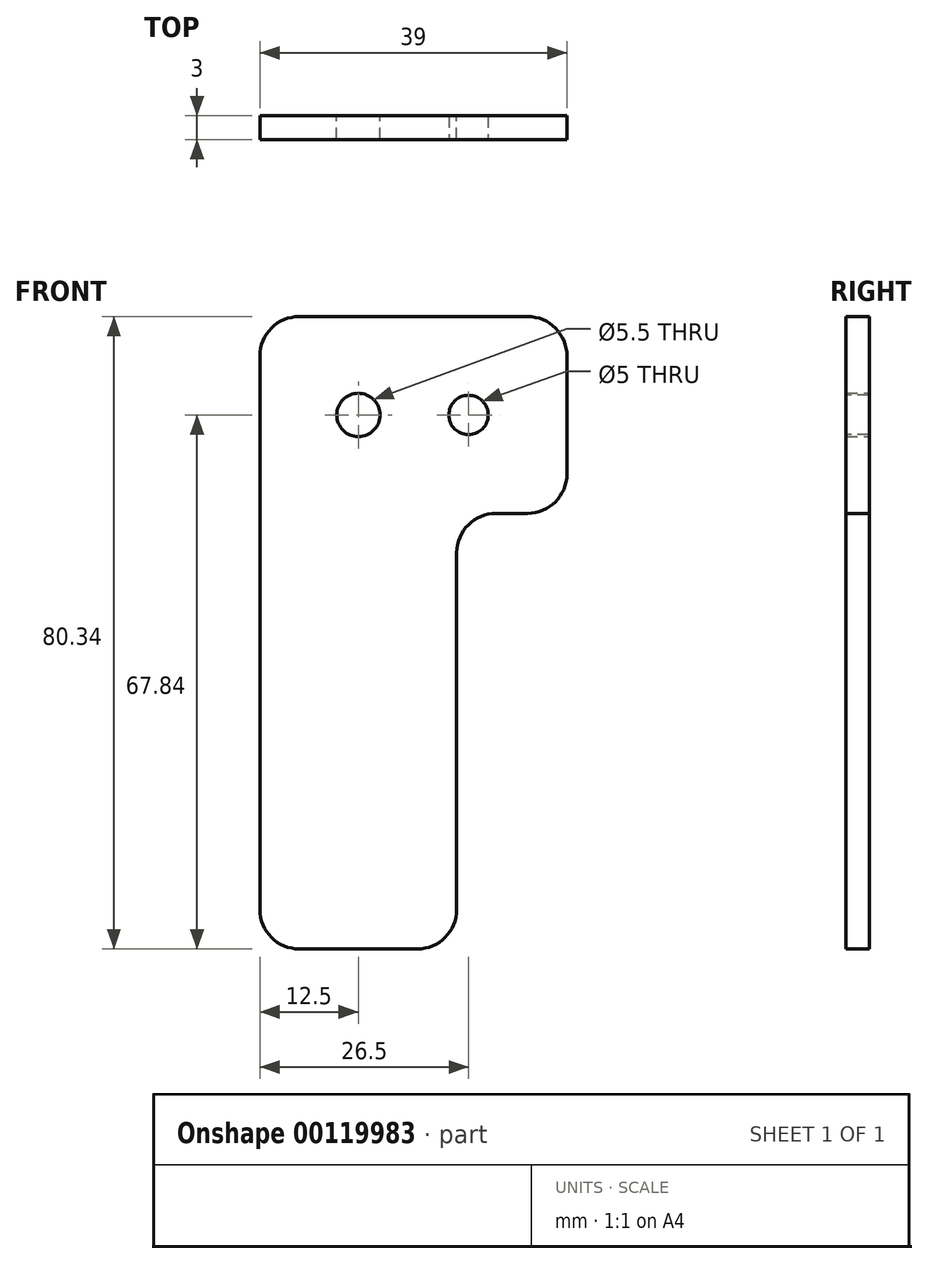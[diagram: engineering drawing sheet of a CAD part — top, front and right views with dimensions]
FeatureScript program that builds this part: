
annotation { "Feature Type Name" : "Feature", "Feature Type Description" : "" }
export const myFeature = defineFeature(function(context is Context, id is Id, definition is map)
    precondition{}
    {
        {
            var Q0;
            Q0=qCreatedBy(makeId("Front.planeOp"),FACE);
            var sketch = newSketch(context, id + "F0", { "sketchPlane" : qUnion([Q0])});
            skCircle(sketch, "E0", {"center": v(0, 0) * mm, "radius": 12.5 * mm});
            skLineSegment(sketch, "E1", {"start": v(-12.5, 0) * mm, "end": v(-12.5, -67.84) * mm});
            skLineSegment(sketch, "E2", {"start": v(12.5, -59.32) * mm, "end": v(12.5, 0) * mm});
            skLineSegment(sketch, "E3", {"start": v(12.46, 1) * mm, "end": v(12.46, -1) * mm});
            skLineSegment(sketch, "E4.1.2", {"start": v(-12.46, -1) * mm, "end": v(-12.46, 1) * mm});
            skLineSegment(sketch, "E4.1.3", {"start": v(-12.5, 0) * mm, "end": v(-14.5, 0) * mm});
            skLineSegment(sketch, "E4.anchor1", {"start": v(0, 0) * mm, "end": v(12.46, -1) * mm, "construction": true});
            skLineSegment(sketch, "E4.anchor2", {"start": v(0, 0) * mm, "end": v(-12.46, 1) * mm, "construction": true});
            skPoint(sketch, "E5.visualSharp", {"position": v(-12.5, -70) * mm});
            skCircle(sketch, "E6", {"center": v(0, 0) * mm, "radius": 1.5 * mm});
            skLineSegment(sketch, "E7", {"start": v(-12.5, -67.84) * mm, "end": v(12.5, -67.84) * mm});
            skLineSegment(sketch, "E8", {"start": v(12.5, -67.84) * mm, "end": v(12.5, -59.32) * mm});
            skLineSegment(sketch, "E9", {"start": v(-12.5, 0) * mm, "end": v(-12.5, 12.5) * mm});
            skLineSegment(sketch, "E10", {"start": v(-12.5, 12.5) * mm, "end": v(0, 12.5) * mm});
            skLineSegment(sketch, "E11", {"start": v(0, 12.5) * mm, "end": v(12.5, 12.5) * mm});
            skLineSegment(sketch, "E12", {"start": v(12.5, 12.5) * mm, "end": v(12.5, 0) * mm});
            skLineSegment(sketch, "E13.bottom", {"start": v(12.5, 12.5) * mm, "end": v(26.5, 12.5) * mm});
            skLineSegment(sketch, "E13.top", {"start": v(12.5, -12.5) * mm, "end": v(26.5, -12.5) * mm});
            skLineSegment(sketch, "E13.left", {"start": v(12.5, 12.5) * mm, "end": v(12.5, -12.5) * mm});
            skLineSegment(sketch, "E13.right", {"start": v(26.5, 12.5) * mm, "end": v(26.5, -12.5) * mm});
            skSolve(sketch);
        }
        {
            var Q0;
            Q0=qSketchRegion(id+"F0",true);
            var Q1;
            Q1=makeQuery(id+"F0.imprint","IMPRINT",FACE,{"disambiguationData":[TD([[makeQuery(id+"F0.imprint","IMPRINT",EDGE,{"derivedFrom":sQuery(id+"F0.wireOp",EDGE,"E6")}),1.0]])]});
            extrude(context, id + "F1", {"entities" : qUnion([Q0, Q1]), "depth" : 3 * mm});
        }
        {
            var Q0;
            Q0=makeQuery(id+"F1.opExtrude","CAP_FACE",FACE,{"disambiguationData":[OSD([sQuery(id+"F0.wireOp",EDGE,"E0"),sQuery(id+"F0.wireOp",EDGE,"E1"),sQuery(id+"F0.wireOp",EDGE,"JVscDJdW-LMbe-N2Un-CdBq-hpjq6N3PD5wY"),sQuery(id+"F0.wireOp",EDGE,"DDVEh3Pz-a52C-6xJS-MlhY-Dl9SJFHWTEuZ"),sQuery(id+"F0.wireOp",EDGE,"Qa6hpvG3-VeAc-d2hB-WOSB-8mIrRalq00KK"),sQuery(id+"F0.wireOp",EDGE,"E2"),sQuery(id+"F0.wireOp",EDGE,"P5pQIiWr-d6a9-dL8I-5OkA-PKon0IUBUqMW"),sQuery(id+"F0.wireOp",EDGE,"O7sfM2wC-z6aj-ywW9-o4Z8-QTpTmjdLFcAP"),sQuery(id+"F0.wireOp",EDGE,"E4.1.0"),sQuery(id+"F0.wireOp",EDGE,"E4.1.1"),sQuery(id+"F0.wireOp",EDGE,"E4.2.0"),sQuery(id+"F0.wireOp",EDGE,"E4.2.1"),sQuery(id+"F0.wireOp",EDGE,"E4.3.0"),sQuery(id+"F0.wireOp",EDGE,"E4.3.1"),sQuery(id+"F0.wireOp",EDGE,"E4.4.0"),sQuery(id+"F0.wireOp",EDGE,"E4.4.1"),sQuery(id+"F0.wireOp",EDGE,"E4.5.0"),sQuery(id+"F0.wireOp",EDGE,"E4.5.1"),sQuery(id+"F0.wireOp",EDGE,"E4.6.0"),sQuery(id+"F0.wireOp",EDGE,"E4.6.1"),sQuery(id+"F0.wireOp",EDGE,"E4.7.0"),sQuery(id+"F0.wireOp",EDGE,"E4.7.1"),sQuery(id+"F0.wireOp",EDGE,"E4.8.0"),sQuery(id+"F0.wireOp",EDGE,"E4.8.1"),sQuery(id+"F0.wireOp",EDGE,"E4.9.0"),sQuery(id+"F0.wireOp",EDGE,"E4.9.1"),sQuery(id+"F0.wireOp",EDGE,"E4.10.0"),sQuery(id+"F0.wireOp",EDGE,"E4.10.1"),sQuery(id+"F0.wireOp",EDGE,"E4.11.0"),sQuery(id+"F0.wireOp",EDGE,"E4.11.1"),sQuery(id+"F0.wireOp",EDGE,"E4.12.0"),sQuery(id+"F0.wireOp",EDGE,"E4.12.1"),sQuery(id+"F0.wireOp",EDGE,"E4.13.0"),sQuery(id+"F0.wireOp",EDGE,"E4.13.1"),sQuery(id+"F0.wireOp",EDGE,"E4.14.0"),sQuery(id+"F0.wireOp",EDGE,"E4.14.1"),sQuery(id+"F0.wireOp",EDGE,"E4.15.0"),sQuery(id+"F0.wireOp",EDGE,"E4.15.1"),sQuery(id+"F0.wireOp",EDGE,"E4.16.0"),sQuery(id+"F0.wireOp",EDGE,"E4.16.1"),sQuery(id+"F0.wireOp",EDGE,"E4.17.0"),sQuery(id+"F0.wireOp",EDGE,"E4.17.1"),sQuery(id+"F0.wireOp",EDGE,"E4.18.0"),sQuery(id+"F0.wireOp",EDGE,"E4.18.1"),sQuery(id+"F0.wireOp",EDGE,"E4.19.0"),sQuery(id+"F0.wireOp",EDGE,"E4.19.1"),sQuery(id+"F0.wireOp",EDGE,"77a9c1b7-26f3-49d6-a4df-445b79814aa3.filletArc"),sQuery(id+"F0.wireOp",EDGE,"E5.filletArc"),sQuery(id+"F0.wireOp",EDGE,"49b3b11a-55af-475c-928b-22e7df24001a.filletArc"),sQuery(id+"F0.wireOp",EDGE,"1ca6fddc-51b8-416d-a5db-f5d9bfdd4f67.filletArc")])],"isStart":false});
            var sketch = newSketch(context, id + "F2", { "sketchPlane" : qUnion([Q0])});
            skLineSegment(sketch, "E14", {"start": v(0, 0) * mm, "end": v(0, -5) * mm});
            skLineSegment(sketch, "E15", {"start": v(0, -5) * mm, "end": v(0, -13.5) * mm});
            skCircle(sketch, "E16", {"center": v(0, -13.5) * mm, "radius": 1.5 * mm});
            skCircle(sketch, "E17", {"center": v(0, -5) * mm, "radius": 1.5 * mm});
            skSolve(sketch);
        }
        {
            var Q0;
            Q0=makeQuery(id+"F2.imprint","IMPRINT",FACE,{"disambiguationData":[TD([[makeQuery(id+"F2.imprint","IMPRINT",EDGE,{"derivedFrom":sQuery(id+"F2.wireOp",EDGE,"E16")}),-1.0]])]});
            var sketch = newSketch(context, id + "F3", { "sketchPlane" : qUnion([Q0])});
            skCircle(sketch, "E18", {"center": v(0, 0) * mm, "radius": 2.75 * mm});
            skSolve(sketch);
        }
        {
            var Q0;
            Q0 = qSketchRegion(id + "F3", true);
            extrude(context, id + "F4", {"entities" : qUnion([Q0]), "operationType" : NewBodyOperationType.REMOVE, "depth" : 762 * mm, "symmetric" : true});
        }
        {
            var Q0;
            Q0=qCreatedBy(makeId("Front.planeOp"),FACE);
            var sketch = newSketch(context, id + "F5", { "sketchPlane" : qUnion([Q0])});
            skPoint(sketch, "E19", {"position": v(-12.46, 1.02) * mm});
            skPoint(sketch, "E20", {"position": v(0, 0) * mm});
            skLineSegment(sketch, "E21", {"start": v(-12.46, 1.02) * mm, "end": v(0, 0) * mm});
            skSolve(sketch);
        }
        {
            var Q0;
            Q0=makeQuery(id+"F1.opExtrude","SWEPT_EDGE",EDGE,{"disambiguationData":[OSD([sQuery(id+"F0.wireOp",EDGE,"E7"),sQuery(id+"F0.wireOp",EDGE,"E8")])]});
            var Q1;
            Q1=makeQuery(id+"F1.opExtrude","SWEPT_EDGE",EDGE,{"disambiguationData":[OSD([sQuery(id+"F0.wireOp",EDGE,"E1"),sQuery(id+"F0.wireOp",EDGE,"E7")])]});
            var Q2;
            Q2=makeQuery(id+"F1.opExtrude","SWEPT_EDGE",EDGE,{"disambiguationData":[OSD([sQuery(id+"F0.wireOp",EDGE,"E9"),sQuery(id+"F0.wireOp",EDGE,"E10")])]});
            var Q3;
            Q3=makeQuery(id+"F1.opExtrude","SWEPT_EDGE",EDGE,{"disambiguationData":[OSD([sQuery(id+"F0.wireOp",EDGE,"E2"),sQuery(id+"F0.wireOp",EDGE,"E13.top"),sQuery(id+"F0.wireOp",EDGE,"E13.left")])]});
            var Q4;
            Q4=makeQuery(id+"F1.opExtrude","SWEPT_EDGE",EDGE,{"disambiguationData":[OSD([sQuery(id+"F0.wireOp",EDGE,"E13.top"),sQuery(id+"F0.wireOp",EDGE,"E13.right")])]});
            var Q5;
            Q5=makeQuery(id+"F1.opExtrude","SWEPT_EDGE",EDGE,{"disambiguationData":[OSD([sQuery(id+"F0.wireOp",EDGE,"E13.bottom"),sQuery(id+"F0.wireOp",EDGE,"E13.right")])]});
            fillet(context, id + "F6", {"entities" : qUnion([Q0, Q1, Q2, Q3, Q4, Q5]), "radius" : 5 * mm, "tangentPropagation" : true, "allowEdgeOverflow" : false});
        }
        {
            var Q0;
            Q0=makeQuery(id+"F1.opExtrude","CAP_FACE",FACE,{"disambiguationData":[OSD([sQuery(id+"F0.wireOp",EDGE,"E0"),sQuery(id+"F0.wireOp",EDGE,"E1"),sQuery(id+"F0.wireOp",EDGE,"E2"),sQuery(id+"F0.wireOp",EDGE,"E3"),sQuery(id+"F0.wireOp",EDGE,"E7"),sQuery(id+"F0.wireOp",EDGE,"E8"),sQuery(id+"F0.wireOp",EDGE,"E9"),sQuery(id+"F0.wireOp",EDGE,"E10"),sQuery(id+"F0.wireOp",EDGE,"E11"),sQuery(id+"F0.wireOp",EDGE,"E13.bottom"),sQuery(id+"F0.wireOp",EDGE,"E13.top"),sQuery(id+"F0.wireOp",EDGE,"E13.right")])],"isStart":false});
            var sketch = newSketch(context, id + "F7", { "sketchPlane" : qUnion([Q0])});
            skCircle(sketch, "E22", {"center": v(14, 0) * mm, "radius": 2.5 * mm});
            skSolve(sketch);
        }
        {
            var Q0;
            Q0=makeQuery(id+"F7.imprint","IMPRINT",FACE,{"disambiguationData":[TD([[makeQuery(id+"F7.imprint","IMPRINT",EDGE,{"derivedFrom":sQuery(id+"F7.wireOp",EDGE,"E22")}),1.0]])]});
            extrude(context, id + "F8", {"entities" : qUnion([Q0]), "operationType" : NewBodyOperationType.REMOVE, "oppositeDirection" : true, "depth" : 25 * mm});
        }
    });
